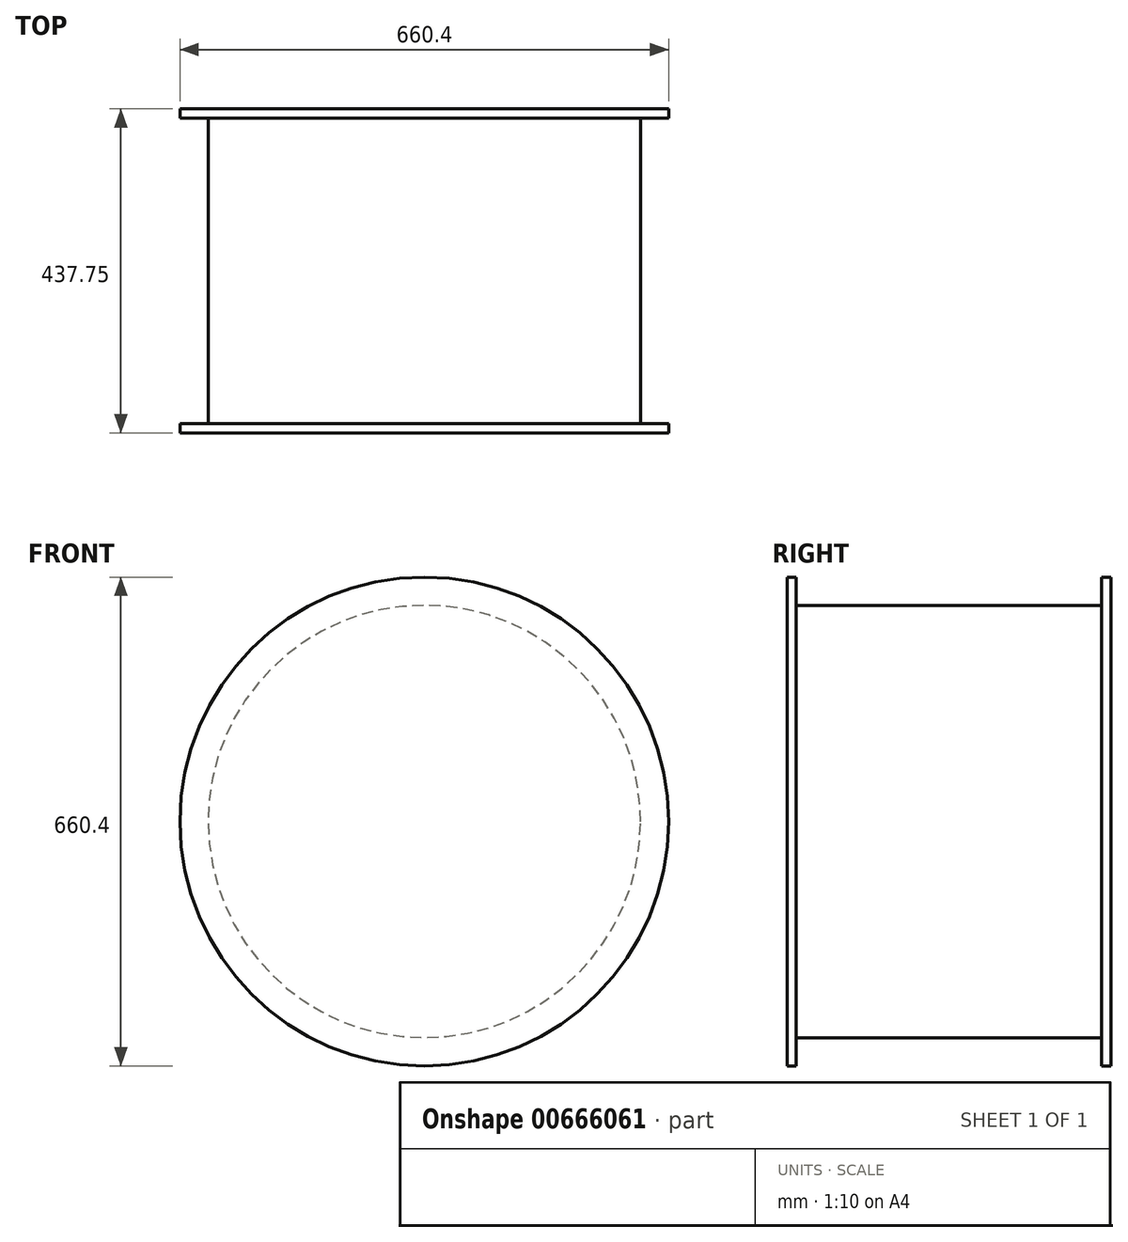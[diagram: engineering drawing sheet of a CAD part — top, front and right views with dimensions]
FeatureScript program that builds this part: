
annotation { "Feature Type Name" : "Feature", "Feature Type Description" : "" }
export const myFeature = defineFeature(function(context is Context, id is Id, definition is map)
    precondition{}
    {
        {
            var Q0;
            Q0=qCreatedBy(makeId("Front.planeOp"),FACE);
            var sketch = newSketch(context, id + "F0", { "sketchPlane" : qUnion([Q0])});
            skCircle(sketch, "E0", {"center": v(0, 0) * mm, "radius": 330.2 * mm});
            skSolve(sketch);
        }
        {
            var Q0;
            Q0 = qSketchRegion(id + "F0", true);
            extrude(context, id + "F1", {"entities" : qUnion([Q0]), "depth" : 12.5 * mm, "offsetDistance" : 25 * mm});
        }
        {
            var Q0;
            Q0=makeQuery(id+"F1.opExtrude","CAP_FACE",FACE,{"disambiguationData":[OSD([sQuery(id+"F0.wireOp",EDGE,"E0")])],"isStart":false});
            var sketch = newSketch(context, id + "F2", { "sketchPlane" : qUnion([Q0])});
            skCircle(sketch, "E1", {"center": v(0, 0) * mm, "radius": 292.1 * mm});
            skSolve(sketch);
        }
        {
            var Q0;
            Q0 = qSketchRegion(id + "F2", true);
            extrude(context, id + "F3", {"entities" : qUnion([Q0]), "operationType" : NewBodyOperationType.ADD, "depth" : 412.75 * mm, "offsetDistance" : 25 * mm});
        }
        {
            var Q0;
            Q0=makeQuery(id+"F3.opExtrude","CAP_FACE",FACE,{"disambiguationData":[OSD([sQuery(id+"F2.wireOp",EDGE,"E1")])],"isStart":false});
            var sketch = newSketch(context, id + "F4", { "sketchPlane" : qUnion([Q0])});
            skCircle(sketch, "E2", {"center": v(0, 0) * mm, "radius": 330.2 * mm});
            skSolve(sketch);
        }
        {
            var Q0;
            Q0=makeQuery(id+"F4.imprint","IMPRINT",FACE,{"disambiguationData":[TD([[makeQuery(id+"F4.imprint","IMPRINT",EDGE,{"derivedFrom":sQuery(id+"F4.wireOp",EDGE,"E2")}),1.0]])]});
            var Q1;
            Q1=makeQuery(id+"F4.imprint","IMPRINT",FACE,{"disambiguationData":[TD([[makeQuery(id+"F4.imprint","IMPRINT",EDGE,{"derivedFrom":makeQuery(id+"F3.opExtrude","CAP_EDGE",EDGE,{"disambiguationData":[OSD([sQuery(id+"F2.wireOp",EDGE,"E1")])],"isStart":false})}),1.0]])]});
            var Q2;
            Q2=sQuery(id+"F4.wireOp",EDGE,"E2");
            extrude(context, id + "F5", {"entities" : qUnion([Q0, Q1]), "surfaceEntities" : qUnion([Q2]), "depth" : 12.5 * mm, "offsetDistance" : 25 * mm});
        }
    });
